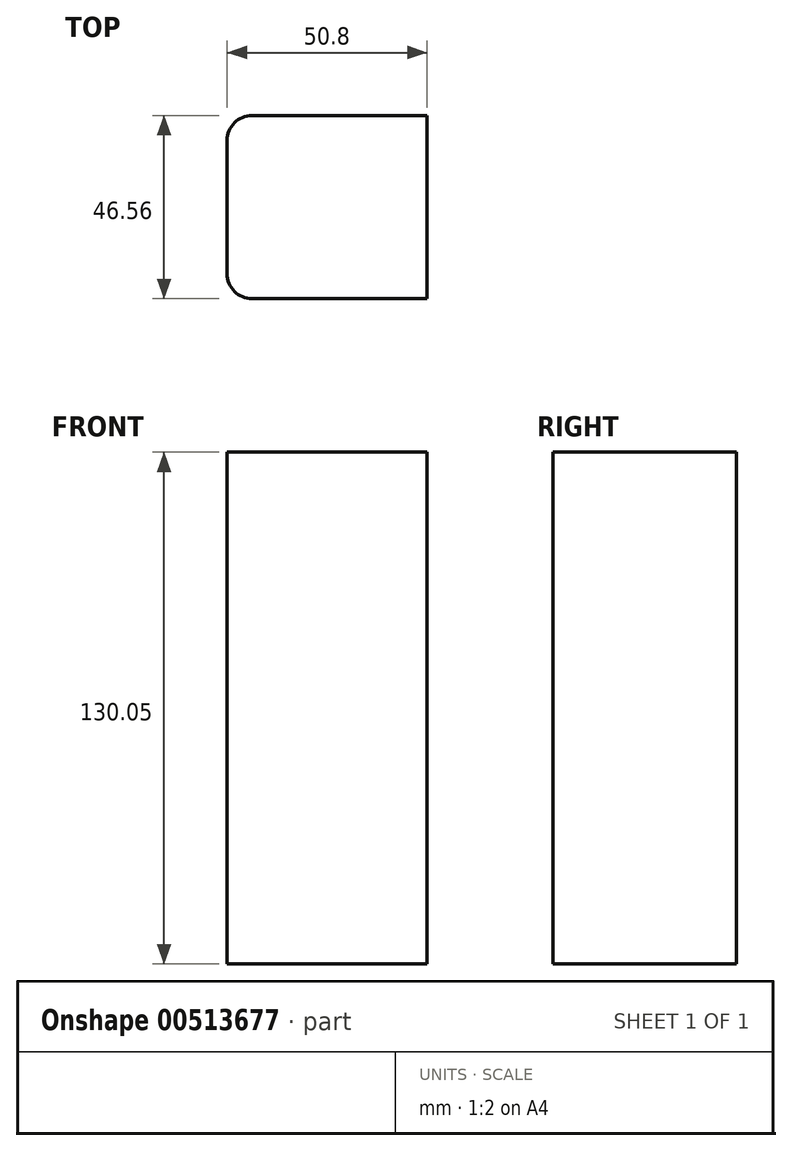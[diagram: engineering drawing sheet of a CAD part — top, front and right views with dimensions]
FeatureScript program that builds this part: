
annotation { "Feature Type Name" : "Feature", "Feature Type Description" : "" }
export const myFeature = defineFeature(function(context is Context, id is Id, definition is map)
    precondition{}
    {
        {
            var Q0;
            Q0=qCreatedBy(makeId("Top.planeOp"),FACE);
            var sketch = newSketch(context, id + "F0", { "sketchPlane" : qUnion([Q0])});
            skLineSegment(sketch, "E0.bottom", {"start": v(25.4, 23.28) * mm, "end": v(-19.05, 23.28) * mm});
            skLineSegment(sketch, "E0.top", {"start": v(25.4, -23.28) * mm, "end": v(-19.05, -23.28) * mm});
            skLineSegment(sketch, "E0.left", {"start": v(25.4, 23.28) * mm, "end": v(25.4, -23.28) * mm});
            skLineSegment(sketch, "E0.right", {"start": v(-25.4, 16.93) * mm, "end": v(-25.4, -16.93) * mm});
            skPoint(sketch, "E0.middle", {"position": v(0, 0) * mm});
            skPoint(sketch, "E1.visualSharp", {"position": v(-25.4, -23.28) * mm});
            skArc(sketch, "E1.filletArc", {"start": v(-25.4, -16.93) * mm, "mid": v(-23.54, -21.42) * mm, "end": v(-19.05, -23.28) * mm});
            skPoint(sketch, "E2.visualSharp", {"position": v(-25.4, 23.28) * mm});
            skArc(sketch, "E2.filletArc", {"start": v(-19.05, 23.28) * mm, "mid": v(-23.54, 21.42) * mm, "end": v(-25.4, 16.93) * mm});
            skSolve(sketch);
        }
        {
            var Q0;
            Q0 = qSketchRegion(id + "F0", true);
            extrude(context, id + "F1", {"entities" : qUnion([Q0]), "depth" : 130.05 * mm});
        }
    });
